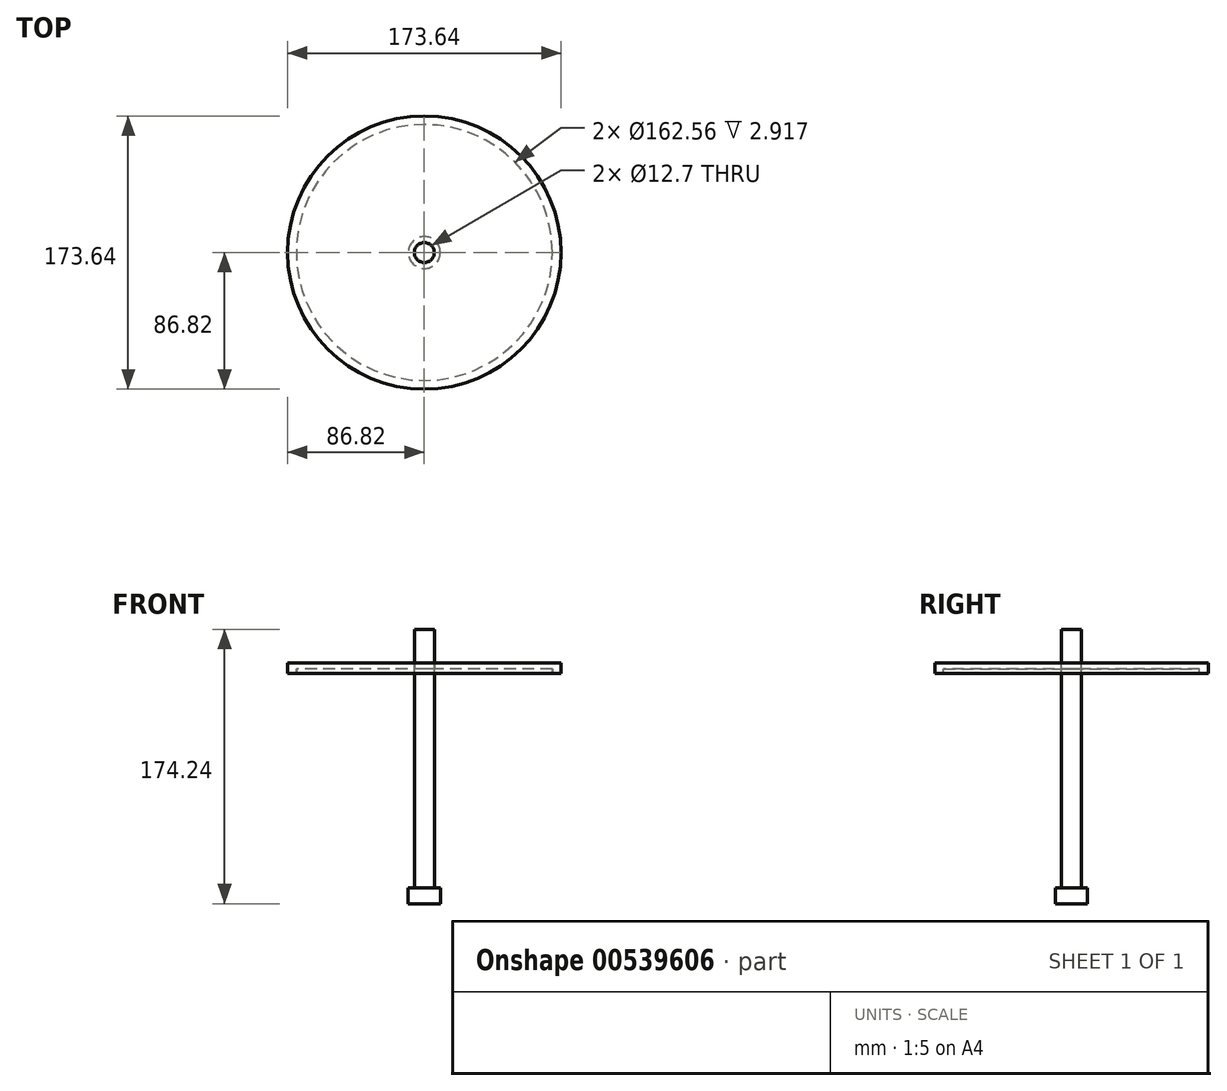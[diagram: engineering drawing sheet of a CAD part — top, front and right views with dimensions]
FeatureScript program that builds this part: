
annotation { "Feature Type Name" : "Feature", "Feature Type Description" : "" }
export const myFeature = defineFeature(function(context is Context, id is Id, definition is map)
    precondition{}
    {
        {
            var Q0;
            Q0=qCreatedBy(makeId("Front.planeOp"),FACE);
            var sketch = newSketch(context, id + "F0", { "sketchPlane" : qUnion([Q0])});
            skLineSegment(sketch, "E0", {"start": v(0, 76.2) * mm, "end": v(0, -76.2) * mm});
            skLineSegment(sketch, "E1", {"start": v(0, 76.2) * mm, "end": v(-81.28, 76.2) * mm});
            skLineSegment(sketch, "E2", {"start": v(-81.28, 76.2) * mm, "end": v(-76.2, -76.2) * mm});
            skLineSegment(sketch, "E3", {"start": v(-76.2, -76.2) * mm, "end": v(0, -76.2) * mm});
            skArc(sketch, "E4", {"start": v(-76.3, -73) * mm, "mid": v(-75.3, -75.27) * mm, "end": v(-73, -76.2) * mm});
            skLineSegment(sketch, "E5", {"start": v(-73, -72.9) * mm, "end": v(0, -72.9) * mm});
            skLineSegment(sketch, "E6", {"start": v(-73, -72.9) * mm, "end": v(-77.98, 76.2) * mm});
            skLineSegment(sketch, "E7", {"start": v(0, 80) * mm, "end": v(-86.82, 80.01) * mm});
            skLineSegment(sketch, "E8", {"start": v(-86.82, 80.01) * mm, "end": v(-86.82, 73.28) * mm});
            skLineSegment(sketch, "E9", {"start": v(-86.82, 73.28) * mm, "end": v(-81.28, 73.28) * mm});
            skLineSegment(sketch, "E10", {"start": v(-81.28, 73.28) * mm, "end": v(-81.28, 76.2) * mm});
            skLineSegment(sketch, "E11", {"start": v(0, 76.2) * mm, "end": v(0, 80) * mm});
            skLineSegment(sketch, "E12", {"start": v(0, 101.34) * mm, "end": v(-6.35, 101.34) * mm});
            skLineSegment(sketch, "E13", {"start": v(-6.35, 101.34) * mm, "end": v(-6.35, -72.9) * mm});
            skLineSegment(sketch, "E14", {"start": v(-6.35, -72.9) * mm, "end": v(0, -72.9) * mm});
            skLineSegment(sketch, "E15", {"start": v(0, -72.9) * mm, "end": v(0, 101.34) * mm});
            skLineSegment(sketch, "E16", {"start": v(-10.16, -72.9) * mm, "end": v(-10.16, -62.74) * mm});
            skLineSegment(sketch, "E17", {"start": v(-10.16, -62.74) * mm, "end": v(-6.35, -62.74) * mm});
            skSolve(sketch);
        }
        {
            var Q0;
            {var subQ1=sQuery(id+"F0.wireOp",EDGE,"E0");Q0=makeQuery(id+"F0.imprint","IMPRINT",FACE,{"disambiguationData":[TD([[makeQuery(id+"F0.imprint","IMPRINT",EDGE,{"derivedFrom":subQ1}),-1.0]])]});}
            var Q1;
            {var subQ3=sQuery(id+"F0.wireOp",EDGE,"E16");Q1=makeQuery(id+"F0.imprint","IMPRINT",FACE,{"disambiguationData":[TD([[makeQuery(id+"F0.imprint","IMPRINT",EDGE,{"derivedFrom":subQ3}),-1.0]])]});}
            var Q2;
            Q2=sQuery(id+"F0.wireOp",EDGE,"E0");
            revolve(context, id + "F1", {"entities" : qUnion([Q0, Q1]), "axis" : qUnion([Q2]), "revolveType" : RevolveType.FULL});
        }
        {
            var Q0;
            {var subQ0=sQuery(id+"F0.wireOp",EDGE,"E8");Q0=makeQuery(id+"F0.imprint","IMPRINT",FACE,{"disambiguationData":[TD([[makeQuery(id+"F0.imprint","IMPRINT",EDGE,{"derivedFrom":subQ0}),1.0]])]});}
            var Q1;
            Q1=sQuery(id+"F0.wireOp",EDGE,"E0");
            revolve(context, id + "F2", {"entities" : qUnion([Q0]), "axis" : qUnion([Q1]), "revolveType" : RevolveType.FULL});
        }
        {
            var Q0;
            {var subQ5=sQuery(id+"F0.wireOp",EDGE,"E12");Q0=makeQuery(id+"F0.imprint","IMPRINT",FACE,{"disambiguationData":[TD([[makeQuery(id+"F0.imprint","IMPRINT",EDGE,{"derivedFrom":subQ5}),1.0]])]});}
            var Q1;
            {var subQ0=sQuery(id+"F0.wireOp",EDGE,"E15");var subQ1=sQuery(id+"F0.wireOp",EDGE,"E1");var subQ2=makeQuery(id+"F0.imprint","INTERSECT",VERTEX,{"derivedFrom":[subQ1,subQ0]});Q1=makeQuery(id+"F0.imprint","IMPRINT",FACE,{"disambiguationData":[TD([[makeQuery(id+"F0.imprint","IMPRINT",EDGE,{"disambiguationData":[TD([[subQ2,-1.0]])],"derivedFrom":subQ1}),-1.0]])]});}
            var Q2;
            {var subQ0=sQuery(id+"F0.wireOp",EDGE,"E14");Q2=makeQuery(id+"F0.imprint","IMPRINT",FACE,{"disambiguationData":[TD([[makeQuery(id+"F0.imprint","IMPRINT",EDGE,{"derivedFrom":subQ0}),1.0]])]});}
            var Q3;
            Q3=sQuery(id+"F0.wireOp",EDGE,"E15");
            revolve(context, id + "F3", {"entities" : qUnion([Q0, Q1, Q2]), "axis" : qUnion([Q3]), "revolveType" : RevolveType.FULL});
        }
    });
